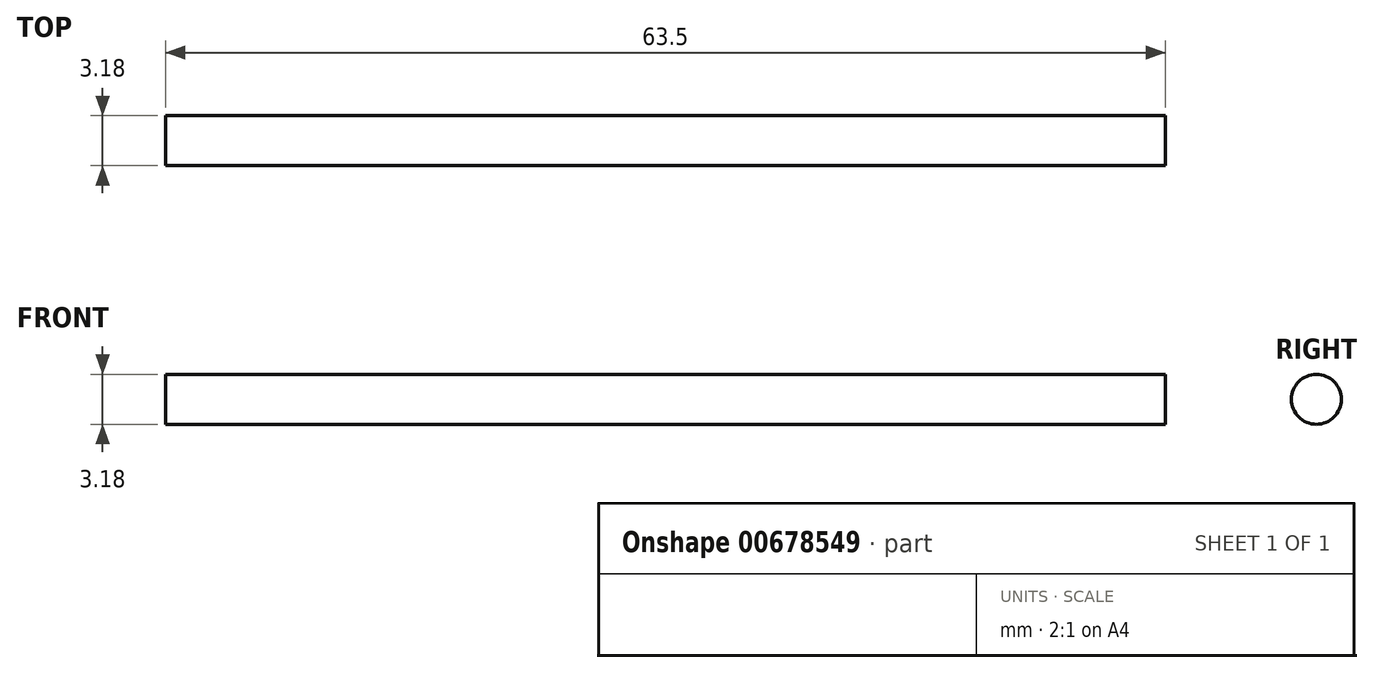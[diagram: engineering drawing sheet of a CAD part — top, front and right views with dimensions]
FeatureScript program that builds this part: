
annotation { "Feature Type Name" : "Feature", "Feature Type Description" : "" }
export const myFeature = defineFeature(function(context is Context, id is Id, definition is map)
    precondition{}
    {
        {
            var Q0;
            Q0=qCreatedBy(makeId("Right.planeOp"),FACE);
            var sketch = newSketch(context, id + "F0", { "sketchPlane" : qUnion([Q0])});
            skCircle(sketch, "E0", {"center": v(0, 0) * mm, "radius": 1.59 * mm});
            skSolve(sketch);
        }
        {
            var Q0;
            Q0 = qSketchRegion(id + "F0", true);
            extrude(context, id + "F1", {"entities" : qUnion([Q0]), "oppositeDirection" : true, "depth" : 63.5 * mm, "offsetDistance" : 25.4 * mm});
        }
    });
